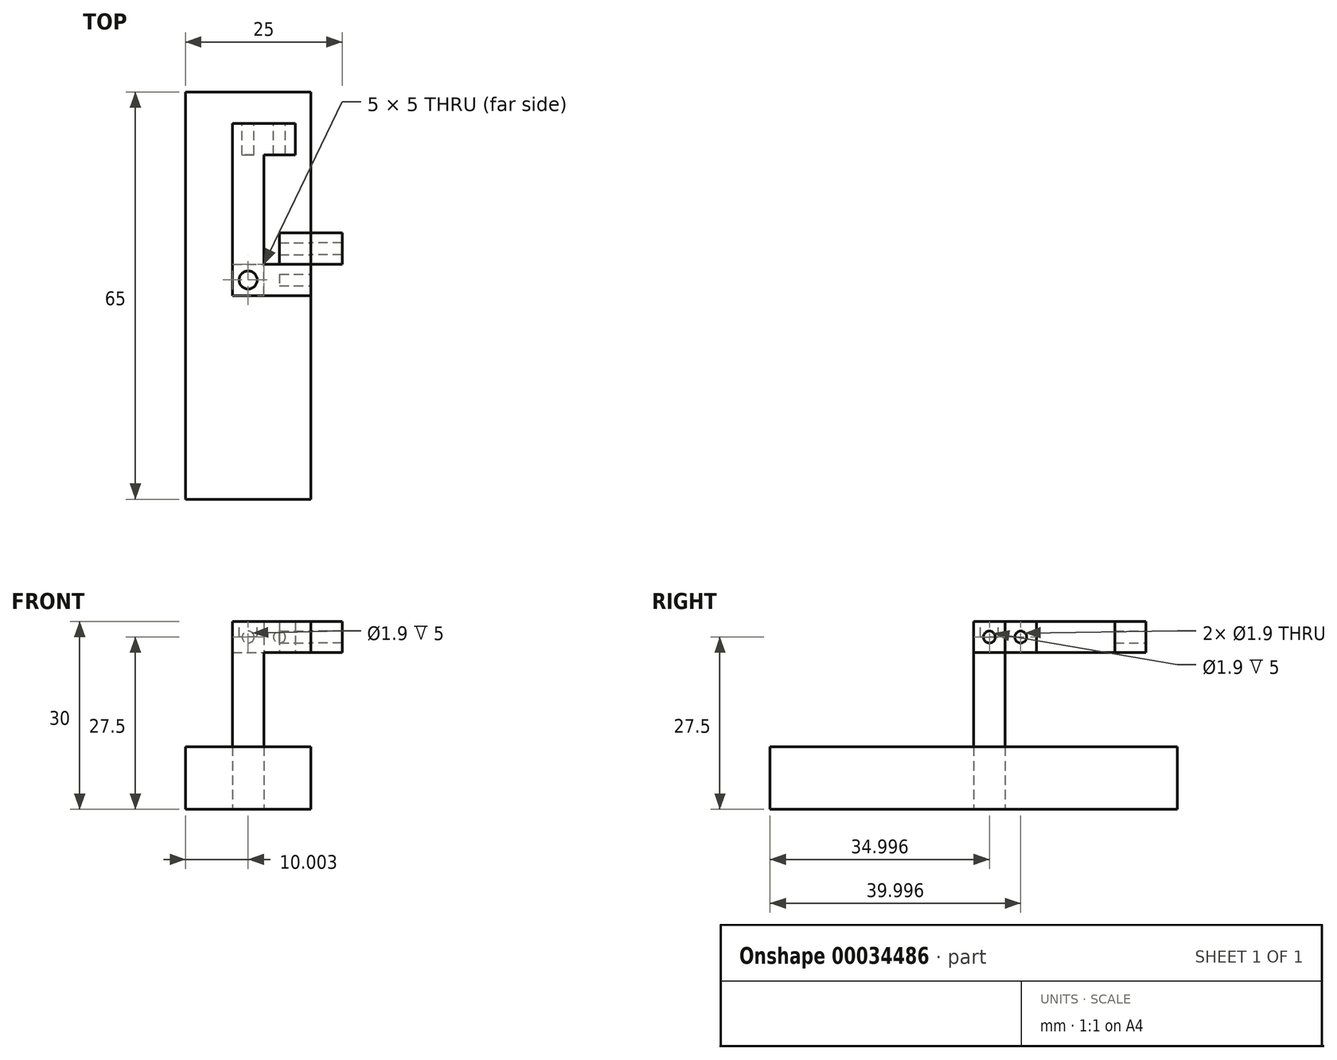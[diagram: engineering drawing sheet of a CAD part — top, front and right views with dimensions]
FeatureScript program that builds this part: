
annotation { "Feature Type Name" : "Feature", "Feature Type Description" : "" }
export const myFeature = defineFeature(function(context is Context, id is Id, definition is map)
    precondition{}
    {
        {
            var Q0;
            Q0=qCreatedBy(makeId("Top.planeOp"),FACE);
            var sketch = newSketch(context, id + "F0", { "sketchPlane" : qUnion([Q0])});
            skLineSegment(sketch, "E0.bottom", {"start": v(-10.84, 44.76) * mm, "end": v(-3.34, 44.76) * mm, "construction": true});
            skLineSegment(sketch, "E0.top", {"start": v(-10.84, -20.24) * mm, "end": v(-3.34, -20.24) * mm, "construction": true});
            skLineSegment(sketch, "E0.left", {"start": v(-10.84, 44.76) * mm, "end": v(-10.84, -20.24) * mm, "construction": true});
            skLineSegment(sketch, "E0.right", {"start": v(9.16, 44.76) * mm, "end": v(9.16, -20.24) * mm, "construction": true});
            skLineSegment(sketch, "E1", {"start": v(-10.84, 24.76) * mm, "end": v(9.16, 24.76) * mm, "construction": true});
            skLineSegment(sketch, "E2", {"start": v(9.16, 4.76) * mm, "end": v(-10.84, 4.76) * mm, "construction": true});
            skLineSegment(sketch, "E3", {"start": v(-10.84, 39.76) * mm, "end": v(9.16, 39.76) * mm, "construction": true});
            skLineSegment(sketch, "E4", {"start": v(4.16, 44.76) * mm, "end": v(4.16, -20.24) * mm, "construction": true});
            skLineSegment(sketch, "E5", {"start": v(-10.84, 17.26) * mm, "end": v(9.16, 17.26) * mm, "construction": true});
            skLineSegment(sketch, "E6", {"start": v(-10.84, 12.26) * mm, "end": v(9.16, 12.26) * mm, "construction": true});
            skLineSegment(sketch, "E7", {"start": v(-3.34, 44.76) * mm, "end": v(-3.34, -20.24) * mm, "construction": true});
            skPoint(sketch, "E8.orphan", {"position": v(-0.84, 44.76) * mm});
            skPoint(sketch, "E9.end.orphan", {"position": v(-0.84, -20.24) * mm});
            skLineSegment(sketch, "E10.trimOffspring", {"start": v(4.16, -20.24) * mm, "end": v(9.16, -20.24) * mm, "construction": true});
            skLineSegment(sketch, "E11", {"start": v(-3.34, -20.24) * mm, "end": v(4.16, -20.24) * mm, "construction": true});
            skLineSegment(sketch, "E12", {"start": v(-3.34, 44.76) * mm, "end": v(4.16, 44.76) * mm, "construction": true});
            skLineSegment(sketch, "E13", {"start": v(1.66, 44.76) * mm, "end": v(1.66, -20.24) * mm, "construction": true});
            skLineSegment(sketch, "E14", {"start": v(-0.84, 44.76) * mm, "end": v(-0.84, -20.24) * mm, "construction": true});
            skLineSegment(sketch, "E15", {"start": v(-10.84, 14.76) * mm, "end": v(9.16, 14.76) * mm, "construction": true});
            skPoint(sketch, "E16.end.orphan", {"position": v(9.16, 44.76) * mm});
            skLineSegment(sketch, "E17", {"start": v(4.16, 44.76) * mm, "end": v(9.16, 44.76) * mm, "construction": true});
            skPoint(sketch, "E18.trimOffspring.end.orphan", {"position": v(-3.34, 39.76) * mm});
            skPoint(sketch, "E19.orphan", {"position": v(4.16, 39.76) * mm});
            skPoint(sketch, "E20.orphan", {"position": v(1.66, 12.26) * mm});
            skPoint(sketch, "E21.trimOffspring.end.orphan", {"position": v(4.16, 12.26) * mm});
            skLineSegment(sketch, "E22", {"start": v(-10.84, 44.76) * mm, "end": v(9.16, 44.76) * mm});
            skLineSegment(sketch, "E23", {"start": v(9.16, -20.24) * mm, "end": v(-10.84, -20.24) * mm});
            skLineSegment(sketch, "E24", {"start": v(9.16, 44.76) * mm, "end": v(9.16, -20.24) * mm});
            skLineSegment(sketch, "E25", {"start": v(-10.84, -20.24) * mm, "end": v(-10.84, 44.76) * mm});
            skLineSegment(sketch, "E26", {"start": v(-3.34, 17.26) * mm, "end": v(1.66, 17.26) * mm});
            skLineSegment(sketch, "E27", {"start": v(1.66, 17.26) * mm, "end": v(1.66, 12.26) * mm});
            skLineSegment(sketch, "E28", {"start": v(-3.34, 12.26) * mm, "end": v(-3.34, 17.26) * mm});
            skLineSegment(sketch, "E29", {"start": v(-3.34, 12.26) * mm, "end": v(1.66, 12.26) * mm});
            skSolve(sketch);
        }
        {
            var Q0;
            Q0 = qSketchRegion(id + "F0", true);
            extrude(context, id + "F1", {"entities" : qUnion([Q0]), "depth" : 10 * mm});
        }
        {
            var Q0;
            Q0=makeQuery(id+"F0.imprint","IMPRINT",FACE,{"disambiguationData":[TD([[makeQuery(id+"F0.imprint","IMPRINT",EDGE,{"derivedFrom":sQuery(id+"F0.wireOp",EDGE,"E26")}),-1.0]])]});
            extrude(context, id + "F2", {"entities" : qUnion([Q0]), "depth" : 30 * mm});
        }
        {
            var Q0;
            Q0=makeQuery(id+"F2.opExtrude","SWEPT_FACE",FACE,{"disambiguationData":[OSD([sQuery(id+"F0.wireOp",EDGE,"E27")])]});
            var sketch = newSketch(context, id + "F3", { "sketchPlane" : qUnion([Q0])});
            skLineSegment(sketch, "E30", {"start": v(12.26, 25) * mm, "end": v(17.26, 25) * mm});
            skLineSegment(sketch, "E31", {"start": v(12.26, 25) * mm, "end": v(12.26, 30) * mm});
            skLineSegment(sketch, "E32", {"start": v(12.26, 30) * mm, "end": v(17.26, 30) * mm});
            skLineSegment(sketch, "E33", {"start": v(17.26, 30) * mm, "end": v(17.26, 25) * mm});
            skSolve(sketch);
        }
        {
            var Q0;
            Q0 = qSketchRegion(id + "F3", true);
            extrude(context, id + "F4", {"entities" : qUnion([Q0]), "operationType" : NewBodyOperationType.ADD, "depth" : 7.5 * mm});
        }
        {
            var Q0;
            Q0=makeQuery(id+"F4.boolean.opBoolean","MERGE",FACE,{"derivedFrom":[makeQuery(id+"F2.opExtrude","SWEPT_FACE",FACE,{"disambiguationData":[OSD([sQuery(id+"F0.wireOp",EDGE,"E26")])]}),makeQuery(id+"F4.opExtrude","SWEPT_FACE",FACE,{"disambiguationData":[OSD([sQuery(id+"F3.wireOp",EDGE,"E33")])]})]});
            var sketch = newSketch(context, id + "F5", { "sketchPlane" : qUnion([Q0])});
            skLineSegment(sketch, "E34.bottom", {"start": v(3.34, 30) * mm, "end": v(-1.66, 30) * mm});
            skLineSegment(sketch, "E34.top", {"start": v(3.34, 25) * mm, "end": v(-1.66, 25) * mm});
            skLineSegment(sketch, "E34.left", {"start": v(3.34, 30) * mm, "end": v(3.34, 25) * mm});
            skLineSegment(sketch, "E34.right", {"start": v(-1.66, 30) * mm, "end": v(-1.66, 25) * mm});
            skSolve(sketch);
        }
        {
            var Q0;
            Q0 = qSketchRegion(id + "F5", true);
            extrude(context, id + "F6", {"entities" : qUnion([Q0]), "operationType" : NewBodyOperationType.ADD, "depth" : 22.5 * mm});
        }
        {
            var Q0;
            Q0=makeQuery(id+"F6.boolean.opBoolean","MERGE",FACE,{"derivedFrom":[makeQuery(id+"F4.boolean.opBoolean","MERGE",FACE,{"derivedFrom":[makeQuery(id+"F2.opExtrude","CAP_FACE",FACE,{"disambiguationData":[OSD([sQuery(id+"F0.wireOp",EDGE,"E26"),sQuery(id+"F0.wireOp",EDGE,"E27"),sQuery(id+"F0.wireOp",EDGE,"E28"),sQuery(id+"F0.wireOp",EDGE,"E29")])],"isStart":false}),makeQuery(id+"F4.opExtrude","SWEPT_FACE",FACE,{"disambiguationData":[OSD([sQuery(id+"F3.wireOp",EDGE,"E32")])]})]}),makeQuery(id+"F6.opExtrude","SWEPT_FACE",FACE,{"disambiguationData":[OSD([sQuery(id+"F5.wireOp",EDGE,"E34.bottom")])]})]});
            var sketch = newSketch(context, id + "F7", { "sketchPlane" : qUnion([Q0])});
            skLineSegment(sketch, "E35", {"start": v(1.66, 17.26) * mm, "end": v(-3.34, 12.26) * mm, "construction": true});
            skCircle(sketch, "E36", {"center": v(-0.84, 14.76) * mm, "radius": 1.45 * mm});
            skSolve(sketch);
        }
        {
            var Q0;
            Q0 = qSketchRegion(id + "F7", true);
            extrude(context, id + "F8", {"entities" : qUnion([Q0]), "operationType" : NewBodyOperationType.REMOVE, "oppositeDirection" : true, "depth" : 2.5 * mm});
        }
        {
            var Q0;
            Q0=makeQuery(id+"F6.opExtrude","CAP_FACE",FACE,{"disambiguationData":[OSD([sQuery(id+"F5.wireOp",EDGE,"E34.bottom"),sQuery(id+"F5.wireOp",EDGE,"E34.top"),sQuery(id+"F5.wireOp",EDGE,"E34.left"),sQuery(id+"F5.wireOp",EDGE,"E34.right")])],"isStart":false});
            var sketch = newSketch(context, id + "F9", { "sketchPlane" : qUnion([Q0])});
            skLineSegment(sketch, "E37", {"start": v(3.34, 25) * mm, "end": v(-1.66, 30) * mm, "construction": true});
            skCircle(sketch, "E38", {"center": v(0.84, 27.5) * mm, "radius": 0.95 * mm});
            skSolve(sketch);
        }
        {
            var Q0;
            Q0 = qSketchRegion(id + "F9", true);
            extrude(context, id + "F10", {"entities" : qUnion([Q0]), "operationType" : NewBodyOperationType.REMOVE, "oppositeDirection" : true, "depth" : 5 * mm});
        }
        {
            var Q0;
            Q0=makeQuery(id+"F4.opExtrude","CAP_FACE",FACE,{"disambiguationData":[OSD([sQuery(id+"F3.wireOp",EDGE,"E30"),sQuery(id+"F3.wireOp",EDGE,"E31"),sQuery(id+"F3.wireOp",EDGE,"E32"),sQuery(id+"F3.wireOp",EDGE,"E33")])],"isStart":false});
            var sketch = newSketch(context, id + "F11", { "sketchPlane" : qUnion([Q0])});
            skLineSegment(sketch, "E39", {"start": v(17.26, 25) * mm, "end": v(12.26, 30) * mm, "construction": true});
            skCircle(sketch, "E40", {"center": v(14.76, 27.5) * mm, "radius": 0.95 * mm});
            skSolve(sketch);
        }
        {
            var Q0;
            Q0 = qSketchRegion(id + "F11", true);
            extrude(context, id + "F12", {"entities" : qUnion([Q0]), "operationType" : NewBodyOperationType.REMOVE, "oppositeDirection" : true, "depth" : 5 * mm});
        }
        {
            var Q0;
            {var subQ0=sQuery(id+"F0.wireOp",EDGE,"E26");var subQ1=makeQuery(id+"F2.opExtrude","SWEPT_FACE",FACE,{"disambiguationData":[OSD([subQ0])]});var subQ2=sQuery(id+"F3.wireOp",EDGE,"E33");var subQ3=makeQuery(id+"F4.opExtrude","SWEPT_FACE",FACE,{"disambiguationData":[OSD([subQ2])]});var subQ4=sQuery(id+"F3.wireOp",EDGE,"E32");Q0=makeQuery(id+"F6.boolean.opBoolean","SPLIT",FACE,{"disambiguationData":[TD([makeQuery(id+"F4.opExtrude","SWEPT_FACE",FACE,{"disambiguationData":[OSD([subQ4])]})])],"derivedFrom":makeQuery(id+"F4.boolean.opBoolean","MERGE",FACE,{"derivedFrom":[subQ1,subQ3]})});}
            var sketch = newSketch(context, id + "F13", { "sketchPlane" : qUnion([Q0])});
            skLineSegment(sketch, "E41.bottom", {"start": v(-9.16, 30) * mm, "end": v(-4.16, 30) * mm});
            skLineSegment(sketch, "E41.top", {"start": v(-9.16, 25) * mm, "end": v(-4.16, 25) * mm});
            skLineSegment(sketch, "E41.left", {"start": v(-9.16, 30) * mm, "end": v(-9.16, 25) * mm});
            skLineSegment(sketch, "E41.right", {"start": v(-4.16, 30) * mm, "end": v(-4.16, 25) * mm});
            skSolve(sketch);
        }
        {
            var Q0;
            Q0=makeQuery(id+"F13.imprint","IMPRINT",FACE,{"disambiguationData":[TD([[makeQuery(id+"F13.imprint","IMPRINT",EDGE,{"derivedFrom":sQuery(id+"F13.wireOp",EDGE,"E41.bottom")}),1.0]])]});
            extrude(context, id + "F14", {"entities" : qUnion([Q0]), "depth" : 5 * mm});
        }
        {
            var Q0;
            Q0=makeQuery(id+"F6.opExtrude","SWEPT_FACE",FACE,{"disambiguationData":[OSD([sQuery(id+"F5.wireOp",EDGE,"E34.right")])]});
            var sketch = newSketch(context, id + "F15", { "sketchPlane" : qUnion([Q0])});
            skLineSegment(sketch, "E42.bottom", {"start": v(39.76, 30) * mm, "end": v(34.76, 30) * mm});
            skLineSegment(sketch, "E42.top", {"start": v(39.76, 25) * mm, "end": v(34.76, 25) * mm});
            skLineSegment(sketch, "E42.left", {"start": v(39.76, 30) * mm, "end": v(39.76, 25) * mm});
            skLineSegment(sketch, "E42.right", {"start": v(34.76, 30) * mm, "end": v(34.76, 25) * mm});
            skSolve(sketch);
        }
        {
            var Q0;
            Q0=makeQuery(id+"F15.imprint","IMPRINT",FACE,{"disambiguationData":[TD([[makeQuery(id+"F15.imprint","IMPRINT",EDGE,{"derivedFrom":sQuery(id+"F15.wireOp",EDGE,"E42.bottom")}),1.0]])]});
            extrude(context, id + "F16", {"entities" : qUnion([Q0]), "operationType" : NewBodyOperationType.ADD, "depth" : 5 * mm});
        }
        {
            var Q0;
            Q0=makeQuery(id+"F14.opExtrude","SWEPT_BODY",BODY,{"disambiguationData":[OSD([sQuery(id+"F13.wireOp",EDGE,"E41.bottom"),sQuery(id+"F13.wireOp",EDGE,"E41.top"),sQuery(id+"F13.wireOp",EDGE,"E41.left"),sQuery(id+"F13.wireOp",EDGE,"E41.right")])]});
            var Q1;
            Q1=makeQuery(id+"F1.opExtrude","SWEPT_BODY",BODY,{"disambiguationData":[OSD([sQuery(id+"F0.wireOp",EDGE,"E22"),sQuery(id+"F0.wireOp",EDGE,"E24"),sQuery(id+"F0.wireOp",EDGE,"E23"),sQuery(id+"F0.wireOp",EDGE,"E25"),sQuery(id+"F0.wireOp",EDGE,"E26"),sQuery(id+"F0.wireOp",EDGE,"E27"),sQuery(id+"F0.wireOp",EDGE,"E28"),sQuery(id+"F0.wireOp",EDGE,"E29")])]});
            booleanBodies(context, id + "F17", {"operationType" : BooleanOperationType.UNION, "tools" : qUnion([Q0, Q1])});
        }
        {
            var Q0;
            Q0=makeQuery(id+"F16.boolean.opBoolean","MERGE",FACE,{"derivedFrom":[makeQuery(id+"F6.opExtrude","CAP_FACE",FACE,{"disambiguationData":[OSD([sQuery(id+"F5.wireOp",EDGE,"E34.bottom"),sQuery(id+"F5.wireOp",EDGE,"E34.top"),sQuery(id+"F5.wireOp",EDGE,"E34.left"),sQuery(id+"F5.wireOp",EDGE,"E34.right")])],"isStart":false}),makeQuery(id+"F16.opExtrude","SWEPT_FACE",FACE,{"disambiguationData":[OSD([sQuery(id+"F15.wireOp",EDGE,"E42.left")])]})]});
            var sketch = newSketch(context, id + "F18", { "sketchPlane" : qUnion([Q0])});
            skLineSegment(sketch, "E43", {"start": v(-1.66, 30) * mm, "end": v(-1.66, 25) * mm, "construction": true});
            skLineSegment(sketch, "E44", {"start": v(-1.66, 25) * mm, "end": v(-6.66, 30) * mm, "construction": true});
            skCircle(sketch, "E45", {"center": v(-4.16, 27.5) * mm, "radius": 0.95 * mm});
            skSolve(sketch);
        }
        {
            var Q0;
            Q0 = qSketchRegion(id + "F18", true);
            extrude(context, id + "F19", {"entities" : qUnion([Q0]), "operationType" : NewBodyOperationType.REMOVE, "oppositeDirection" : true, "depth" : 5 * mm});
        }
        {
            var Q0;
            Q0=makeQuery(id+"F17.opBoolean","MERGE",FACE,{"derivedFrom":[makeQuery(id+"F4.opExtrude","CAP_FACE",FACE,{"disambiguationData":[OSD([sQuery(id+"F3.wireOp",EDGE,"E30"),sQuery(id+"F3.wireOp",EDGE,"E31"),sQuery(id+"F3.wireOp",EDGE,"E32"),sQuery(id+"F3.wireOp",EDGE,"E33")])],"isStart":false}),makeQuery(id+"F14.opExtrude","SWEPT_FACE",FACE,{"disambiguationData":[OSD([sQuery(id+"F13.wireOp",EDGE,"E41.left")])]})]});
            var sketch = newSketch(context, id + "F20", { "sketchPlane" : qUnion([Q0])});
            skLineSegment(sketch, "E46", {"start": v(17.26, 30) * mm, "end": v(17.26, 25) * mm, "construction": true});
            skLineSegment(sketch, "E47", {"start": v(17.26, 30) * mm, "end": v(22.26, 25) * mm, "construction": true});
            skCircle(sketch, "E48", {"center": v(19.76, 27.5) * mm, "radius": 0.95 * mm});
            skSolve(sketch);
        }
        {
            var Q0;
            Q0 = qSketchRegion(id + "F20", true);
            extrude(context, id + "F21", {"entities" : qUnion([Q0]), "operationType" : NewBodyOperationType.REMOVE, "oppositeDirection" : true, "depth" : 5 * mm});
        }
        {
            var Q0;
            Q0=makeQuery(id+"F14.opExtrude","SWEPT_BODY",BODY,{"disambiguationData":[OSD([sQuery(id+"F13.wireOp",EDGE,"E41.bottom"),sQuery(id+"F13.wireOp",EDGE,"E41.top"),sQuery(id+"F13.wireOp",EDGE,"E41.left"),sQuery(id+"F13.wireOp",EDGE,"E41.right")])]});
            var Q1;
            Q1=makeQuery(id+"F1.opExtrude","SWEPT_FACE",FACE,{"disambiguationData":[OSD([sQuery(id+"F0.wireOp",EDGE,"E24")])]});
            mirror(context, id + "F22", {"entities" : qUnion([Q0]), "mirrorPlane" : qUnion([Q1])});
        }
    });
